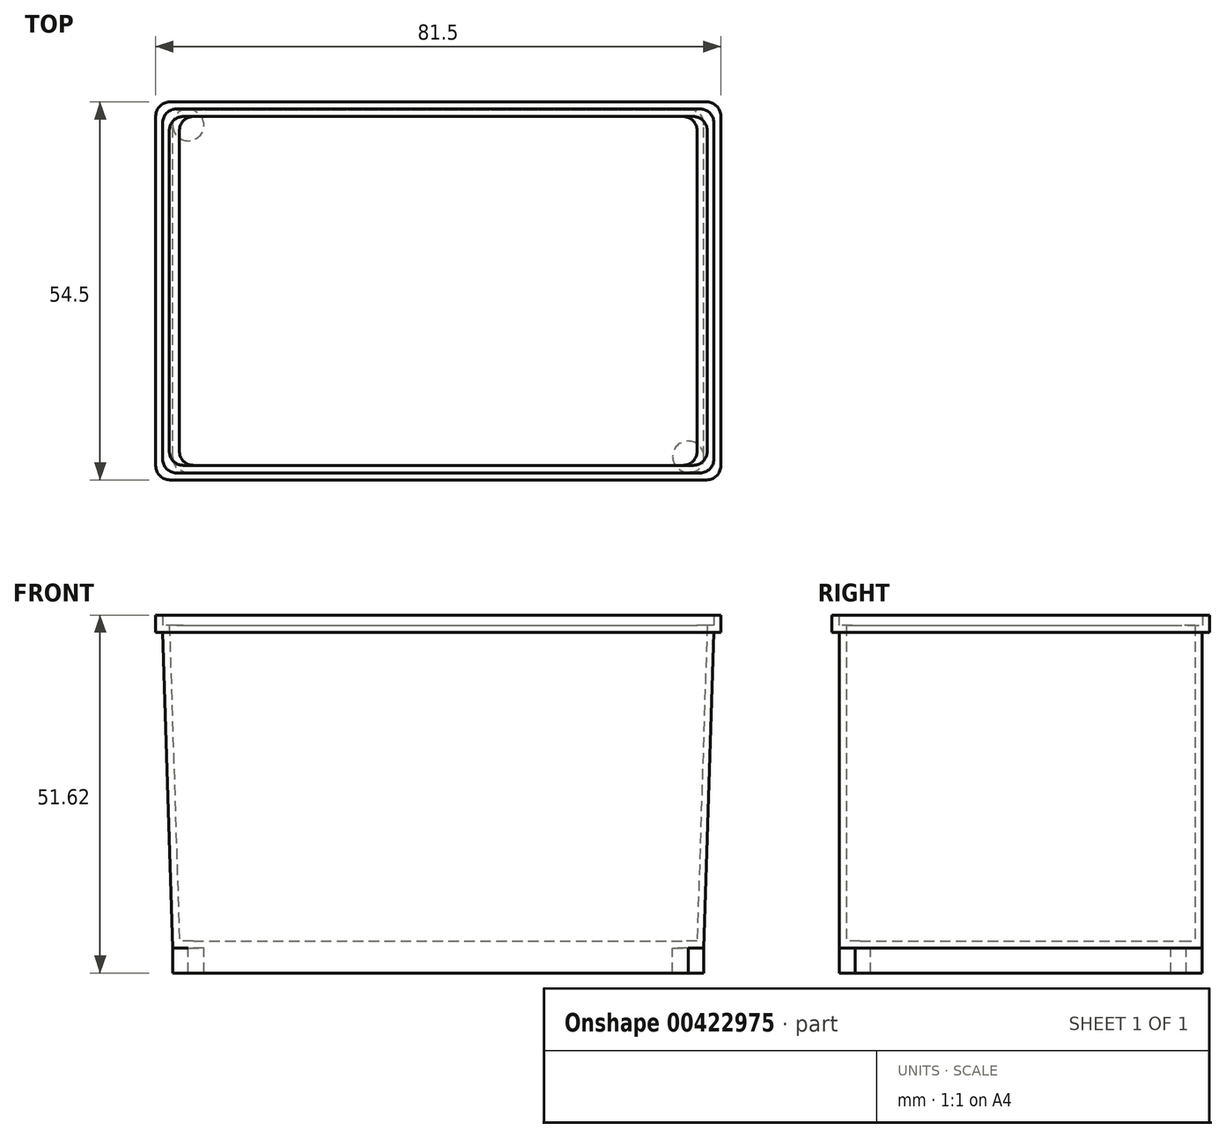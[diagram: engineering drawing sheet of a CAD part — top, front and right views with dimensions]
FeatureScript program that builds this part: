
annotation { "Feature Type Name" : "Feature", "Feature Type Description" : "" }
export const myFeature = defineFeature(function(context is Context, id is Id, definition is map)
    precondition{}
    {
        {
            var Q0;
            Q0=qCreatedBy(makeId("Front.planeOp"),FACE);
            var sketch = newSketch(context, id + "F0", { "sketchPlane" : qUnion([Q0])});
            skLineSegment(sketch, "E0", {"start": v(0, 10.1) * mm, "end": v(-40.75, 10.1) * mm});
            skLineSegment(sketch, "E1", {"start": v(-40.75, 10.1) * mm, "end": v(-40.75, 7.6) * mm});
            skLineSegment(sketch, "E2", {"start": v(-40.75, 7.6) * mm, "end": v(-39.75, 7.6) * mm});
            skLineSegment(sketch, "E3", {"start": v(-39.75, 7.6) * mm, "end": v(-38.3, -37.9) * mm});
            skLineSegment(sketch, "E4", {"start": v(-38.3, -37.9) * mm, "end": v(0, -37.9) * mm});
            skLineSegment(sketch, "E5.MirrorCS", {"start": v(40.75, 7.6) * mm, "end": v(39.75, 7.6) * mm});
            skLineSegment(sketch, "E6.MirrorCS", {"start": v(40.75, 10.1) * mm, "end": v(40.75, 7.6) * mm});
            skLineSegment(sketch, "E7.MirrorCS", {"start": v(39.75, 7.6) * mm, "end": v(38.3, -37.9) * mm});
            skLineSegment(sketch, "E8.MirrorCS", {"start": v(0, 10.1) * mm, "end": v(40.75, 10.1) * mm});
            skLineSegment(sketch, "E9.MirrorCS", {"start": v(38.3, -37.9) * mm, "end": v(0, -37.9) * mm});
            skLineSegment(sketch, "E10", {"start": v(-39.75, 7.6) * mm, "end": v(39.75, 7.6) * mm});
            skSolve(sketch);
        }
        {
            var Q0;
            Q0=makeQuery(id+"F0.imprint","IMPRINT",FACE,{"disambiguationData":[TD([[makeQuery(id+"F0.imprint","IMPRINT",EDGE,{"derivedFrom":sQuery(id+"F0.wireOp",EDGE,"E0")}),1.0]])]});
            extrude(context, id + "F1", {"entities" : qUnion([Q0]), "endBound" : BoundingType.SYMMETRIC, "depth" : 54.5 * mm});
        }
        {
            var Q0;
            Q0=makeQuery(id+"F0.imprint","IMPRINT",FACE,{"disambiguationData":[TD([[makeQuery(id+"F0.imprint","IMPRINT",EDGE,{"derivedFrom":sQuery(id+"F0.wireOp",EDGE,"E3")}),1.0]])]});
            extrude(context, id + "F2", {"entities" : qUnion([Q0]), "operationType" : NewBodyOperationType.ADD, "endBound" : BoundingType.SYMMETRIC, "depth" : 52.3 * mm});
        }
        {
            var Q0;
            Q0=makeQuery(id+"F2.opExtrude","SWEPT_FACE",FACE,{"disambiguationData":[OSD([sQuery(id+"F0.wireOp",EDGE,"E4"),sQuery(id+"F0.wireOp",EDGE,"E9.MirrorCS")])]});
            var sketch = newSketch(context, id + "F3", { "sketchPlane" : qUnion([Q0])});
            skCircle(sketch, "E11", {"center": v(-36.05, 23.9) * mm, "radius": 2.25 * mm});
            skCircle(sketch, "E12.MirrorC", {"center": v(-36.05, -23.9) * mm, "radius": 2.25 * mm});
            skCircle(sketch, "E13.MirrorC", {"center": v(36.05, 23.9) * mm, "radius": 2.25 * mm});
            skCircle(sketch, "E14.MirrorC", {"center": v(36.05, -23.9) * mm, "radius": 2.25 * mm});
            skSolve(sketch);
        }
        {
            var Q0;
            Q0=makeQuery(id+"F1.opExtrude","SWEPT_FACE",FACE,{"disambiguationData":[OSD([sQuery(id+"F0.wireOp",EDGE,"E0"),sQuery(id+"F0.wireOp",EDGE,"E8.MirrorCS")])]});
            shell(context, id + "F4", {"entities" : qUnion([Q0]), "thickness" : 1 * mm});
        }
        {
            var Q0;
            {var subQ0=sQuery(id+"F3.wireOp",EDGE,"E11");var subQ1=sQuery(id+"F0.wireOp",EDGE,"E4");var subQ2=makeQuery(id+"F3.imprint","INTERSECT",VERTEX,{"derivedFrom":[makeQuery(id+"F2.opExtrude","SWEPT_EDGE",EDGE,{"disambiguationData":[OSD([sQuery(id+"F0.wireOp",EDGE,"E3"),subQ1])]}),subQ0]});Q0=makeQuery(id+"F3.imprint","IMPRINT",FACE,{"disambiguationData":[TD([[makeQuery(id+"F3.imprint","IMPRINT",EDGE,{"disambiguationData":[TD([[subQ2,1.0]])],"derivedFrom":subQ0}),1.0]])]});}
            var Q1;
            {var subQ0=sQuery(id+"F3.wireOp",EDGE,"E12.MirrorC");var subQ1=sQuery(id+"F0.wireOp",EDGE,"E4");var subQ2=makeQuery(id+"F3.imprint","INTERSECT",VERTEX,{"derivedFrom":[makeQuery(id+"F2.opExtrude","SWEPT_EDGE",EDGE,{"disambiguationData":[OSD([sQuery(id+"F0.wireOp",EDGE,"E3"),subQ1])]}),subQ0]});Q1=makeQuery(id+"F3.imprint","IMPRINT",FACE,{"disambiguationData":[TD([[makeQuery(id+"F3.imprint","IMPRINT",EDGE,{"disambiguationData":[TD([[subQ2,1.0]])],"derivedFrom":subQ0}),-1.0]])]});}
            var Q2;
            {var subQ0=sQuery(id+"F3.wireOp",EDGE,"E14.MirrorC");var subQ1=sQuery(id+"F0.wireOp",EDGE,"E9.MirrorCS");var subQ2=makeQuery(id+"F3.imprint","INTERSECT",VERTEX,{"derivedFrom":[makeQuery(id+"F2.opExtrude","SWEPT_EDGE",EDGE,{"disambiguationData":[OSD([sQuery(id+"F0.wireOp",EDGE,"E7.MirrorCS"),subQ1])]}),subQ0]});Q2=makeQuery(id+"F3.imprint","IMPRINT",FACE,{"disambiguationData":[TD([[makeQuery(id+"F3.imprint","IMPRINT",EDGE,{"disambiguationData":[TD([[subQ2,1.0]])],"derivedFrom":subQ0}),1.0]])]});}
            var Q3;
            {var subQ0=sQuery(id+"F3.wireOp",EDGE,"E13.MirrorC");var subQ1=sQuery(id+"F0.wireOp",EDGE,"E9.MirrorCS");var subQ2=makeQuery(id+"F3.imprint","INTERSECT",VERTEX,{"derivedFrom":[makeQuery(id+"F2.opExtrude","SWEPT_EDGE",EDGE,{"disambiguationData":[OSD([sQuery(id+"F0.wireOp",EDGE,"E7.MirrorCS"),subQ1])]}),subQ0]});Q3=makeQuery(id+"F3.imprint","IMPRINT",FACE,{"disambiguationData":[TD([[makeQuery(id+"F3.imprint","IMPRINT",EDGE,{"disambiguationData":[TD([[subQ2,1.0]])],"derivedFrom":subQ0}),-1.0]])]});}
            extrude(context, id + "F5", {"entities" : qUnion([Q0, Q1, Q2, Q3]), "operationType" : NewBodyOperationType.ADD, "depth" : 3.62 * mm});
        }
        {
            var Q0;
            Q0=makeQuery(id+"F2.opExtrude","CAP_EDGE",EDGE,{"disambiguationData":[OSD([sQuery(id+"F0.wireOp",EDGE,"E3")])],"isStart":false});
            var Q1;
            Q1=makeQuery(id+"F2.opExtrude","CAP_EDGE",EDGE,{"disambiguationData":[OSD([sQuery(id+"F0.wireOp",EDGE,"E7.MirrorCS")])],"isStart":false});
            var Q2;
            Q2=makeQuery(id+"F2.opExtrude","CAP_EDGE",EDGE,{"disambiguationData":[OSD([sQuery(id+"F0.wireOp",EDGE,"E7.MirrorCS")])],"isStart":true});
            var Q3;
            Q3=makeQuery(id+"F2.opExtrude","CAP_EDGE",EDGE,{"disambiguationData":[OSD([sQuery(id+"F0.wireOp",EDGE,"E3")])],"isStart":true});
            var Q4;
            Q4=makeQuery(id+"F1.opExtrude","CAP_EDGE",EDGE,{"disambiguationData":[OSD([sQuery(id+"F0.wireOp",EDGE,"E1")])],"isStart":true});
            var Q5;
            Q5=makeQuery(id+"F1.opExtrude","CAP_EDGE",EDGE,{"disambiguationData":[OSD([sQuery(id+"F0.wireOp",EDGE,"E1")])],"isStart":false});
            var Q6;
            Q6=makeQuery(id+"F1.opExtrude","CAP_EDGE",EDGE,{"disambiguationData":[OSD([sQuery(id+"F0.wireOp",EDGE,"E6.MirrorCS")])],"isStart":false});
            var Q7;
            Q7=makeQuery(id+"F1.opExtrude","CAP_EDGE",EDGE,{"disambiguationData":[OSD([sQuery(id+"F0.wireOp",EDGE,"E6.MirrorCS")])],"isStart":true});
            var Q8;
            {var subQ0=sQuery(id+"F0.wireOp",EDGE,"E6.MirrorCS");Q8=makeQuery(id+"F4.opShell","OFFSET_EDGE",EDGE,{"disambiguationData":[OSD([subQ0]),TDD([makeQuery(id+"F1.opExtrude","CAP_EDGE",EDGE,{"disambiguationData":[OSD([subQ0])],"isStart":false})])]});}
            var Q9;
            {var subQ0=sQuery(id+"F0.wireOp",EDGE,"E7.MirrorCS");Q9=makeQuery(id+"F4.opShell","OFFSET_EDGE",EDGE,{"disambiguationData":[OSD([subQ0]),TDD([makeQuery(id+"F2.opExtrude","CAP_EDGE",EDGE,{"disambiguationData":[OSD([subQ0])],"isStart":false})])]});}
            var Q10;
            {var subQ0=sQuery(id+"F0.wireOp",EDGE,"E3");Q10=makeQuery(id+"F4.opShell","OFFSET_EDGE",EDGE,{"disambiguationData":[OSD([subQ0]),TDD([makeQuery(id+"F2.opExtrude","CAP_EDGE",EDGE,{"disambiguationData":[OSD([subQ0])],"isStart":false})])]});}
            var Q11;
            {var subQ0=sQuery(id+"F0.wireOp",EDGE,"E1");Q11=makeQuery(id+"F4.opShell","OFFSET_EDGE",EDGE,{"disambiguationData":[OSD([subQ0]),TDD([makeQuery(id+"F1.opExtrude","CAP_EDGE",EDGE,{"disambiguationData":[OSD([subQ0])],"isStart":false})])]});}
            var Q12;
            {var subQ0=sQuery(id+"F0.wireOp",EDGE,"E3");Q12=makeQuery(id+"F4.opShell","OFFSET_EDGE",EDGE,{"disambiguationData":[OSD([subQ0]),TDD([makeQuery(id+"F2.opExtrude","CAP_EDGE",EDGE,{"disambiguationData":[OSD([subQ0])],"isStart":true})])]});}
            var Q13;
            {var subQ0=sQuery(id+"F0.wireOp",EDGE,"E1");Q13=makeQuery(id+"F4.opShell","OFFSET_EDGE",EDGE,{"disambiguationData":[OSD([subQ0]),TDD([makeQuery(id+"F1.opExtrude","CAP_EDGE",EDGE,{"disambiguationData":[OSD([subQ0])],"isStart":true})])]});}
            var Q14;
            {var subQ0=sQuery(id+"F0.wireOp",EDGE,"E6.MirrorCS");Q14=makeQuery(id+"F4.opShell","OFFSET_EDGE",EDGE,{"disambiguationData":[OSD([subQ0]),TDD([makeQuery(id+"F1.opExtrude","CAP_EDGE",EDGE,{"disambiguationData":[OSD([subQ0])],"isStart":true})])]});}
            var Q15;
            {var subQ0=sQuery(id+"F0.wireOp",EDGE,"E7.MirrorCS");Q15=makeQuery(id+"F4.opShell","OFFSET_EDGE",EDGE,{"disambiguationData":[OSD([subQ0]),TDD([makeQuery(id+"F2.opExtrude","CAP_EDGE",EDGE,{"disambiguationData":[OSD([subQ0])],"isStart":true})])]});}
            fillet(context, id + "F6", {"entities" : qUnion([Q0, Q1, Q2, Q3, Q4, Q5, Q6, Q7, Q8, Q9, Q10, Q11, Q12, Q13, Q14, Q15]), "radius" : 2 * mm, "tangentPropagation" : true, "allowEdgeOverflow" : false});
        }
    });
